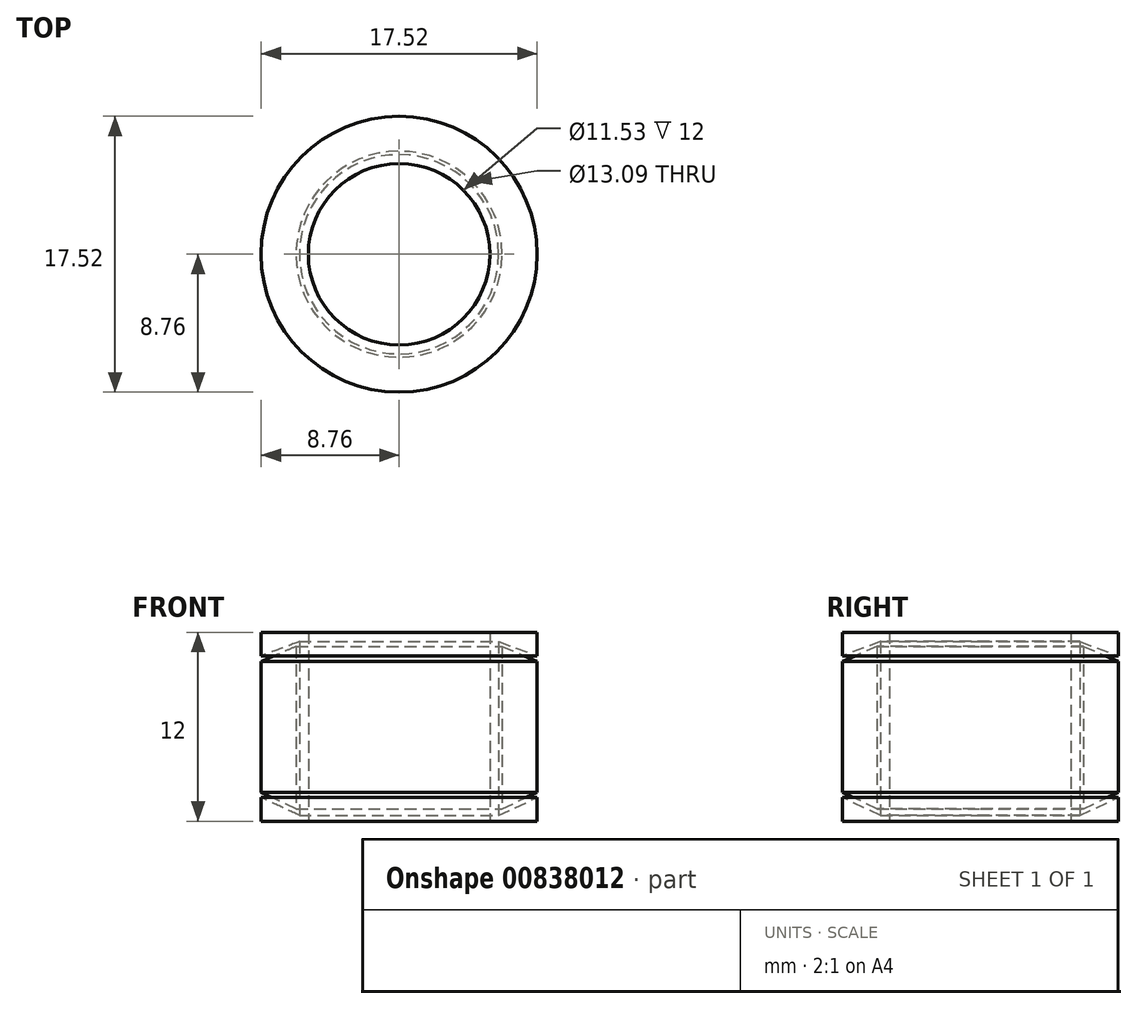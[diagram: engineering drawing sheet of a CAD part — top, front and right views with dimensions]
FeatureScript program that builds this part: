
annotation { "Feature Type Name" : "Feature", "Feature Type Description" : "" }
export const myFeature = defineFeature(function(context is Context, id is Id, definition is map)
    precondition{}
    {
        {
            var Q0;
            Q0=qCreatedBy(makeId("Front.planeOp"),FACE);
            var sketch = newSketch(context, id + "F0", { "sketchPlane" : qUnion([Q0])});
            skLineSegment(sketch, "E0", {"start": v(0, 0) * mm, "end": v(0, 10.05) * mm});
            skLineSegment(sketch, "E1", {"start": v(5.76, 0) * mm, "end": v(5.76, -6) * mm});
            skLineSegment(sketch, "E2", {"start": v(5.76, 0) * mm, "end": v(5.76, 6) * mm});
            skLineSegment(sketch, "E3", {"start": v(5.76, 6) * mm, "end": v(8.76, 6) * mm});
            skLineSegment(sketch, "E4", {"start": v(5.76, -6) * mm, "end": v(8.76, -6) * mm});
            skLineSegment(sketch, "E5", {"start": v(8.76, -6) * mm, "end": v(8.76, -4.5) * mm});
            skLineSegment(sketch, "E6", {"start": v(8.76, 6) * mm, "end": v(8.76, 4.5) * mm});
            skLineSegment(sketch, "E7", {"start": v(8.76, 4.5) * mm, "end": v(6.33, 5.4) * mm});
            skLineSegment(sketch, "E8", {"start": v(6.33, 5.4) * mm, "end": v(6.33, -5.63) * mm});
            skLineSegment(sketch, "E9", {"start": v(6.33, -5.63) * mm, "end": v(8.76, -4.5) * mm});
            skLineSegment(sketch, "E10", {"start": v(8.76, 4.15) * mm, "end": v(8.76, -4.18) * mm});
            skLineSegment(sketch, "E11", {"start": v(8.76, -4.18) * mm, "end": v(6.55, -5.2) * mm});
            skLineSegment(sketch, "E12", {"start": v(6.55, -5.2) * mm, "end": v(6.55, 5.1) * mm});
            skLineSegment(sketch, "E13", {"start": v(6.55, 5.1) * mm, "end": v(8.76, 4.15) * mm});
            skSolve(sketch);
        }
        {
            var Q0;
            Q0 = qSketchRegion(id + "F0", true);
            var Q1;
            Q1=sQuery(id+"F0.wireOp",EDGE,"E0");
            revolve(context, id + "F1", {"surfaceOperationType" : NewSurfaceOperationType.NEW, "entities" : qUnion([Q0]), "axis" : qUnion([Q1]), "revolveType" : RevolveType.FULL});
        }
    });
